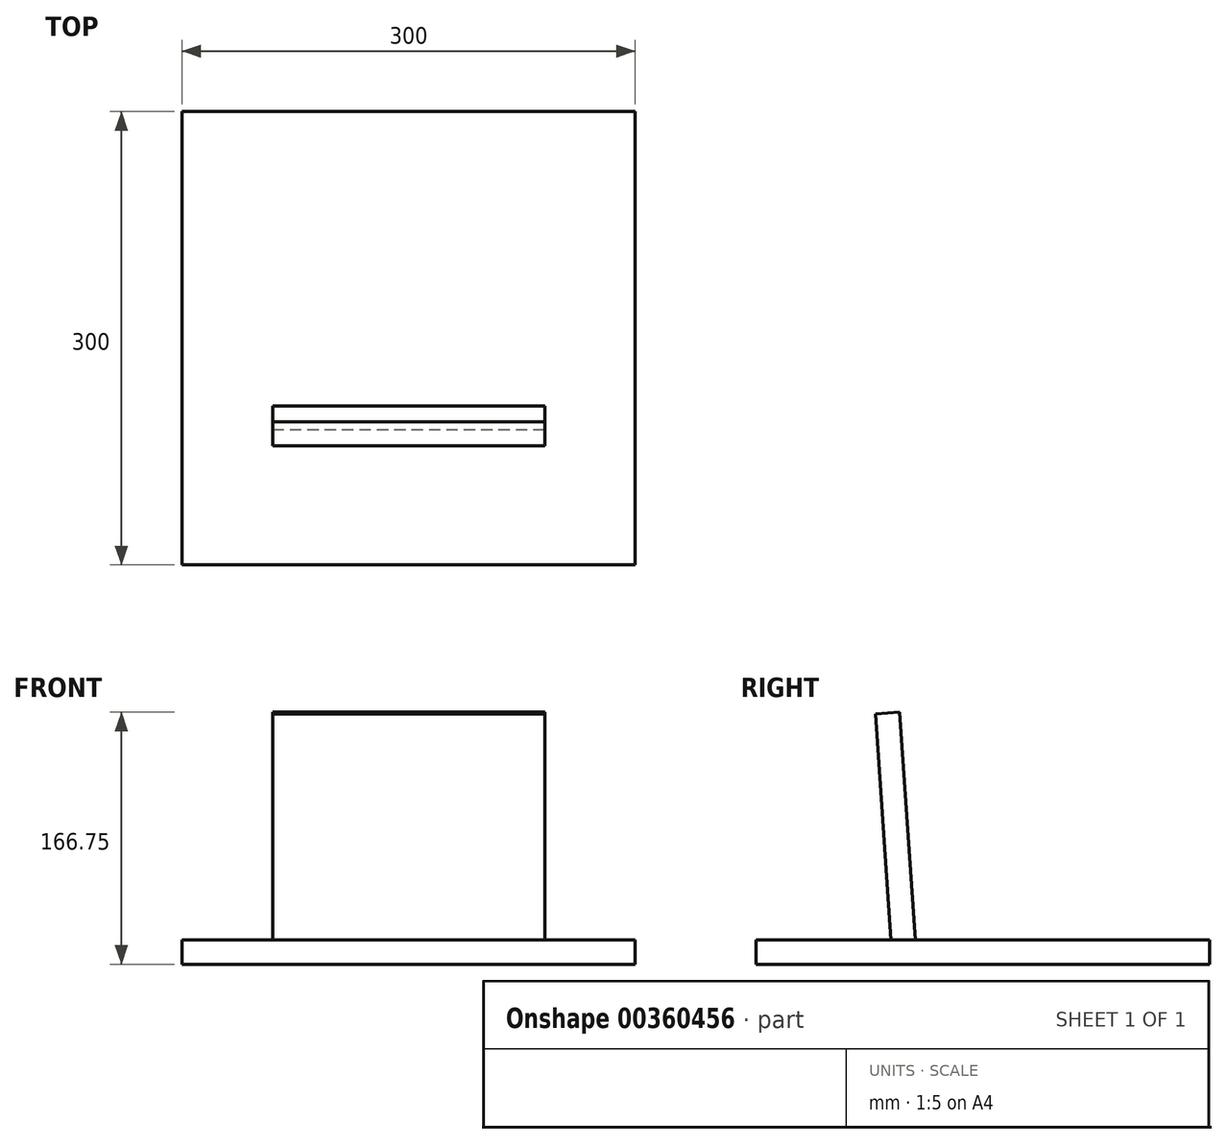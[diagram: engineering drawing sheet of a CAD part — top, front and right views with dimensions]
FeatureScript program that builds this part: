
annotation { "Feature Type Name" : "Feature", "Feature Type Description" : "" }
export const myFeature = defineFeature(function(context is Context, id is Id, definition is map)
    precondition{}
    {
        {
            var Q0;
            Q0=qCreatedBy(makeId("Right.planeOp"),FACE);
            var sketch = newSketch(context, id + "F0", { "sketchPlane" : qUnion([Q0])});
            skLineSegment(sketch, "E0.bottom", {"start": v(150, -8) * mm, "end": v(-150, -8) * mm});
            skLineSegment(sketch, "E0.top", {"start": v(150, 8) * mm, "end": v(-150, 8) * mm});
            skLineSegment(sketch, "E0.left", {"start": v(150, -8) * mm, "end": v(150, 8) * mm});
            skLineSegment(sketch, "E0.right", {"start": v(-150, -8) * mm, "end": v(-150, 8) * mm});
            skPoint(sketch, "E0.middle", {"position": v(0, 0) * mm});
            skLineSegment(sketch, "E1", {"start": v(-0.11, -0.46) * mm, "end": v(0, 223.6) * mm, "construction": true});
            skLineSegment(sketch, "E2", {"start": v(-60.77, 8) * mm, "end": v(-71.23, 157.63) * mm});
            skLineSegment(sketch, "E3", {"start": v(-71.23, 157.63) * mm, "end": v(-55.27, 158.75) * mm});
            skLineSegment(sketch, "E4", {"start": v(-55.27, 158.75) * mm, "end": v(-44.73, 8) * mm});
            skLineSegment(sketch, "E5", {"start": v(-50, 83.38) * mm, "end": v(0, 83.35) * mm, "construction": true});
            skSolve(sketch);
        }
        {
            var Q0;
            Q0=makeQuery(id+"F0.imprint","IMPRINT",FACE,{"disambiguationData":[TD([[makeQuery(id+"F0.imprint","IMPRINT",EDGE,{"derivedFrom":sQuery(id+"F0.wireOp",EDGE,"E0.bottom")}),-1.0]])]});
            extrude(context, id + "F1", {"entities" : qUnion([Q0]), "endBound" : BoundingType.SYMMETRIC, "depth" : 300 * mm});
        }
        {
            var Q0;
            {var subQ0=sQuery(id+"F0.wireOp",EDGE,"E2");Q0=makeQuery(id+"F0.imprint","IMPRINT",FACE,{"disambiguationData":[TD([[makeQuery(id+"F0.imprint","IMPRINT",EDGE,{"derivedFrom":subQ0}),-1.0]])]});}
            extrude(context, id + "F2", {"entities" : qUnion([Q0]), "operationType" : NewBodyOperationType.ADD, "endBound" : BoundingType.SYMMETRIC, "depth" : 180 * mm});
        }
    });
